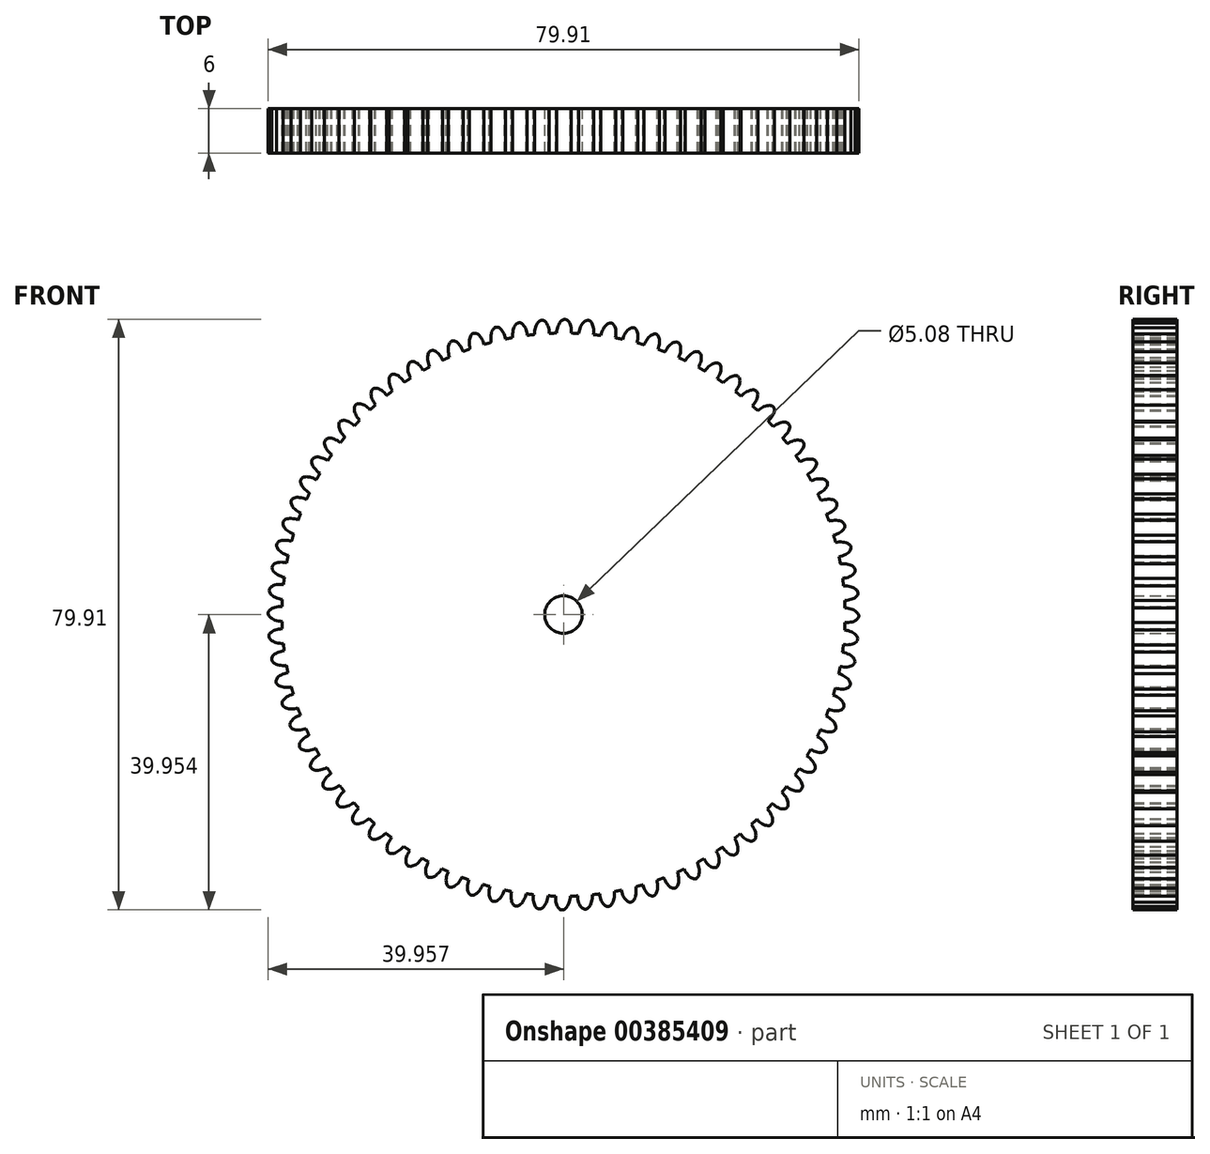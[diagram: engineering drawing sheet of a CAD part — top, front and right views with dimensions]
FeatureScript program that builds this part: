
annotation { "Feature Type Name" : "Feature", "Feature Type Description" : "" }
export const myFeature = defineFeature(function(context is Context, id is Id, definition is map)
    precondition{}
    {
        {
            var Q0;
            Q0=qCreatedBy(makeId("Front.planeOp"),FACE);
            var sketch = newSketch(context, id + "F0", { "sketchPlane" : qUnion([Q0])});
            skCircle(sketch, "E0", {"center": v(1.48, -19.42) * mm, "radius": 38.1 * mm});
            skCircle(sketch, "E1", {"center": v(1.48, -19.42) * mm, "radius": 2.54 * mm});
            skEllipticalArc(sketch, "E2", {});
            skEllipticalArc(sketch, "E3.1.0", {});
            skEllipticalArc(sketch, "E3.2.0", {});
            skEllipticalArc(sketch, "E3.3.0", {});
            skEllipticalArc(sketch, "E3.4.0", {});
            skEllipticalArc(sketch, "E3.5.0", {});
            skEllipticalArc(sketch, "E3.6.0", {});
            skEllipticalArc(sketch, "E3.7.0", {});
            skEllipticalArc(sketch, "E3.8.0", {});
            skEllipticalArc(sketch, "E3.9.0", {});
            skEllipticalArc(sketch, "E3.10.0", {});
            skEllipticalArc(sketch, "E3.11.0", {});
            skEllipticalArc(sketch, "E3.12.0", {});
            skEllipticalArc(sketch, "E3.13.0", {});
            skEllipticalArc(sketch, "E3.14.0", {});
            skEllipticalArc(sketch, "E3.15.0", {});
            skEllipticalArc(sketch, "E3.16.0", {});
            skEllipticalArc(sketch, "E3.17.0", {});
            skEllipticalArc(sketch, "E3.18.0", {});
            skEllipticalArc(sketch, "E3.19.0", {});
            skEllipticalArc(sketch, "E3.20.0", {});
            skEllipticalArc(sketch, "E3.21.0", {});
            skEllipticalArc(sketch, "E3.22.0", {});
            skEllipticalArc(sketch, "E3.23.0", {});
            skEllipticalArc(sketch, "E3.24.0", {});
            skEllipticalArc(sketch, "E3.25.0", {});
            skEllipticalArc(sketch, "E3.26.0", {});
            skEllipticalArc(sketch, "E3.27.0", {});
            skEllipticalArc(sketch, "E3.28.0", {});
            skEllipticalArc(sketch, "E3.29.0", {});
            skEllipticalArc(sketch, "E3.30.0", {});
            skEllipticalArc(sketch, "E3.31.0", {});
            skEllipticalArc(sketch, "E3.32.0", {});
            skEllipticalArc(sketch, "E3.33.0", {});
            skEllipticalArc(sketch, "E3.34.0", {});
            skEllipticalArc(sketch, "E3.35.0", {});
            skEllipticalArc(sketch, "E3.36.0", {});
            skEllipticalArc(sketch, "E3.37.0", {});
            skEllipticalArc(sketch, "E3.38.0", {});
            skEllipticalArc(sketch, "E3.39.0", {});
            skEllipticalArc(sketch, "E3.40.0", {});
            skEllipticalArc(sketch, "E3.41.0", {});
            skEllipticalArc(sketch, "E3.42.0", {});
            skEllipticalArc(sketch, "E3.43.0", {});
            skEllipticalArc(sketch, "E3.44.0", {});
            skEllipticalArc(sketch, "E3.45.0", {});
            skEllipticalArc(sketch, "E3.46.0", {});
            skEllipticalArc(sketch, "E3.47.0", {});
            skEllipticalArc(sketch, "E3.48.0", {});
            skEllipticalArc(sketch, "E3.49.0", {});
            skEllipticalArc(sketch, "E3.50.0", {});
            skEllipticalArc(sketch, "E3.51.0", {});
            skEllipticalArc(sketch, "E3.52.0", {});
            skEllipticalArc(sketch, "E3.53.0", {});
            skEllipticalArc(sketch, "E3.54.0", {});
            skEllipticalArc(sketch, "E3.55.0", {});
            skEllipticalArc(sketch, "E3.56.0", {});
            skEllipticalArc(sketch, "E3.57.0", {});
            skEllipticalArc(sketch, "E3.58.0", {});
            skEllipticalArc(sketch, "E3.59.0", {});
            skEllipticalArc(sketch, "E3.60.0", {});
            skEllipticalArc(sketch, "E3.61.0", {});
            skEllipticalArc(sketch, "E3.62.0", {});
            skEllipticalArc(sketch, "E3.63.0", {});
            skEllipticalArc(sketch, "E3.64.0", {});
            skEllipticalArc(sketch, "E3.65.0", {});
            skEllipticalArc(sketch, "E3.66.0", {});
            skEllipticalArc(sketch, "E3.67.0", {});
            skEllipticalArc(sketch, "E3.68.0", {});
            skEllipticalArc(sketch, "E3.69.0", {});
            skEllipticalArc(sketch, "E3.70.0", {});
            skEllipticalArc(sketch, "E3.71.0", {});
            skEllipticalArc(sketch, "E3.72.0", {});
            skEllipticalArc(sketch, "E3.73.0", {});
            skEllipticalArc(sketch, "E3.74.0", {});
            skEllipticalArc(sketch, "E3.75.0", {});
            skEllipticalArc(sketch, "E3.76.0", {});
            skEllipticalArc(sketch, "E3.77.0", {});
            skEllipticalArc(sketch, "E3.78.0", {});
            skEllipticalArc(sketch, "E3.79.0", {});
            const initialGuessF0  = {"E2": [-0.0014344001059815768, 0.018572813303266773, 0, -1, 0.0018570975044160444, 0.0009917459338206558, 1.604712424427073, 4.760295241054115], "E3.1.0": [-0.0044059786382855005, 0.018227300082595467, 0.07845909572784507, -0.996917333733128, 0.0018570975044160444, 0.0009917459338206558, 1.604712424427073, 4.760295241054115], "E3.2.0": [-0.007341288130832645, 0.017649704599345444, 0.15643446504023098, -0.9876883405951378, 0.0018570975044160444, 0.0009917459338206558, 1.604712424427073, 4.760295241054115], "E3.3.0": [-0.010222231424512, 0.016843587921740923, 0.2334453638559055, -0.9723699203976766, 0.0018570975044160444, 0.0009917459338206558, 1.604712424427073, 4.760295241054115], "E3.4.0": [-0.013031046545907171, 0.01581392002716034, 0.3090169943749475, -0.9510565162951535, 0.0018570975044160444, 0.0009917459338206558, 1.604712424427073, 4.760295241054115], "E3.5.0": [-0.015750416215768955, 0.014567049160573092, 0.3826834323650899, -0.9238795325112867, 0.0018570975044160444, 0.0009917459338206558, 1.604712424427073, 4.760295241054115], "E3.6.0": [-0.018363574615800467, 0.013110662695498342, 0.45399049973954686, -0.8910065241883678, 0.0018570975044160444, 0.0009917459338206558, 1.604712424427073, 4.760295241054115], "E3.7.0": [-0.020854410755502168, 0.011453739738790903, 0.522498564715949, -0.8526401643540923, 0.0018570975044160444, 0.0009917459338206558, 1.604712424427073, 4.760295241054115], "E3.8.0": [-0.02320756780178574, 0.009606495771461688, 0.5877852522924732, -0.8090169943749473, 0.0018570975044160444, 0.0009917459338206558, 1.604712424427073, 4.760295241054115], "E3.9.0": [-0.025408537758956712, 0.007580319666840222, 0.6494480483301838, -0.7604059656000308, 0.0018570975044160444, 0.0009917459338206558, 1.604712424427073, 4.760295241054115], "E3.10.0": [-0.027443750915332344, 0.005387703474383429, 0.7071067811865476, -0.7071067811865475, 0.0018570975044160444, 0.0009917459338206558, 1.604712424427073, 4.760295241054115], "E3.11.0": [-0.02930065950502653, 0.0030421654020366742, 0.7604059656000309, -0.6494480483301837, 0.0018570975044160444, 0.0009917459338206558, 1.604712424427073, 4.760295241054115], "E3.12.0": [-0.030967815069099056, 0.0005581664719865303, 0.8090169943749476, -0.587785252292473, 0.0018570975044160444, 0.0009917459338206558, 1.604712424427073, 4.760295241054115], "E3.13.0": [-0.032434939039111904, -0.002048978636349773, 0.8526401643540923, -0.5224985647159488, 0.0018570975044160444, 0.0009917459338206558, 1.604712424427073, 4.760295241054115], "E3.14.0": [-0.033692986107921735, -0.004763196006415627, 0.8910065241883679, -0.4539904997395467, 0.0018570975044160444, 0.0009917459338206558, 1.604712424427073, 4.760295241054115], "E3.15.0": [-0.03473419999700624, -0.0075677515855557004, 0.9238795325112867, -0.3826834323650897, 0.0018570975044160444, 0.0009917459338206558, 1.604712424427073, 4.760295241054115], "E3.16.0": [-0.035552161276500446, -0.010445354356015239, 0.9510565162951538, -0.3090169943749474, 0.0018570975044160444, 0.0009917459338206558, 1.604712424427073, 4.760295241054115], "E3.17.0": [-0.03614182694311655, -0.013378262939814329, 0.9723699203976768, -0.23344536385590542, 0.0018570975044160444, 0.0009917459338206558, 1.604712424427073, 4.760295241054115], "E3.18.0": [-0.036499561511936146, -0.016348394980242775, 0.9876883405951378, -0.1564344650402308, 0.0018570975044160444, 0.0009917459338206558, 1.604712424427073, 4.760295241054115], "E3.19.0": [-0.03662315943038362, -0.019337438625602218, 0.996917333733128, -0.07845909572784487, 0.0018570975044160444, 0.0009917459338206558, 1.604712424427073, 4.760295241054115], "E3.20.0": [-0.03651185867619128, -0.022326965427861133, 1, 0, 0.0018570975044160444, 0.0009917459338206558, 1.604712424427073, 4.760295241054115], "E3.21.0": [-0.03616634545551997, -0.025298543960165055, 0.996917333733128, 0.078459095727845, 0.0018570975044160444, 0.0009917459338206558, 1.604712424427073, 4.760295241054115], "E3.22.0": [-0.03558874997226995, -0.02823385345271219, 0.9876883405951378, 0.1564344650402307, 0.0018570975044160444, 0.0009917459338206558, 1.604712424427073, 4.760295241054115], "E3.23.0": [-0.03478263329466544, -0.031114796746391556, 0.9723699203976767, 0.23344536385590545, 0.0018570975044160444, 0.0009917459338206558, 1.604712424427073, 4.760295241054115], "E3.24.0": [-0.03375296540008485, -0.033923611867786724, 0.9510565162951536, 0.30901699437494745, 0.0018570975044160444, 0.0009917459338206558, 1.604712424427073, 4.760295241054115], "E3.25.0": [-0.0325060945334976, -0.03664298153764851, 0.9238795325112867, 0.38268343236508984, 0.0018570975044160444, 0.0009917459338206558, 1.604712424427073, 4.760295241054115], "E3.26.0": [-0.031049708068422846, -0.03925613993768002, 0.891006524188368, 0.4539904997395469, 0.0018570975044160444, 0.0009917459338206558, 1.604712424427073, 4.760295241054115], "E3.27.0": [-0.029392785111715412, -0.04174697607738173, 0.8526401643540922, 0.5224985647159489, 0.0018570975044160444, 0.0009917459338206558, 1.604712424427073, 4.760295241054115], "E3.28.0": [-0.027545541144386194, -0.04410013312366529, 0.8090169943749476, 0.5877852522924732, 0.0018570975044160441, 0.0009917459338206556, 1.604712424427073, 4.760295241054115], "E3.29.0": [-0.025519365039764735, -0.046301103080836264, 0.7604059656000309, 0.6494480483301837, 0.0018570975044160444, 0.0009917459338206558, 1.604712424427073, 4.760295241054115], "E3.30.0": [-0.023326748847307933, -0.0483363162372119, 0.7071067811865475, 0.7071067811865476, 0.0018570975044160444, 0.0009917459338206558, 1.604712424427073, 4.760295241054115], "E3.31.0": [-0.02098121077496118, -0.050193224826906094, 0.6494480483301837, 0.760405965600031, 0.0018570975044160444, 0.0009917459338206558, 1.604712424427073, 4.760295241054115], "E3.32.0": [-0.01849721184491104, -0.05186038039097861, 0.5877852522924731, 0.8090169943749475, 0.0018570975044160444, 0.0009917459338206558, 1.604712424427073, 4.760295241054115], "E3.33.0": [-0.015890066736574733, -0.05332750436099146, 0.5224985647159488, 0.8526401643540923, 0.0018570975044160444, 0.0009917459338206558, 1.604712424427073, 4.760295241054115], "E3.34.0": [-0.013175849366508884, -0.054585551429801295, 0.45399049973954675, 0.8910065241883679, 0.0018570975044160444, 0.0009917459338206558, 1.604712424427073, 4.760295241054115], "E3.35.0": [-0.010371293787368807, -0.0556267653188858, 0.3826834323650898, 0.9238795325112867, 0.0018570975044160444, 0.0009917459338206558, 1.604712424427073, 4.760295241054115], "E3.36.0": [-0.00749369101690927, -0.056444726598380006, 0.30901699437494745, 0.9510565162951538, 0.0018570975044160444, 0.0009917459338206558, 1.604712424427073, 4.760295241054115], "E3.37.0": [-0.004560782433110183, -0.05703439226499611, 0.23344536385590542, 0.9723699203976766, 0.0018570975044160444, 0.0009917459338206558, 1.604712424427073, 4.760295241054115], "E3.38.0": [-0.0015906503926817327, -0.0573921268338157, 0.1564344650402309, 0.9876883405951379, 0.0018570975044160444, 0.0009917459338206558, 1.604712424427073, 4.760295241054115], "E3.39.0": [0.0013983932526777068, -0.05751572475226318, 0.07845909572784494, 0.996917333733128, 0.0018570975044160444, 0.0009917459338206558, 1.604712424427073, 4.760295241054115], "E3.40.0": [0.004387920054936623, -0.05740442399807084, 0, 1, 0.0018570975044160444, 0.0009917459338206558, 1.604712424427073, 4.760295241054115], "E3.41.0": [0.0073594985872405295, -0.057058910777399545, -0.0784590957278445, 0.9969173337331281, 0.0018570975044160444, 0.0009917459338206558, 1.604712424427073, 4.760295241054115], "E3.42.0": [0.01029480807978769, -0.0564813152941495, -0.15643446504023084, 0.9876883405951378, 0.0018570975044160444, 0.0009917459338206558, 1.604712424427073, 4.760295241054115], "E3.43.0": [0.013175751373467045, -0.05567519861654499, -0.2334453638559054, 0.9723699203976767, 0.0018570975044160444, 0.0009917459338206558, 1.604712424427073, 4.760295241054115], "E3.44.0": [0.015984566494862205, -0.054645530721964417, -0.309016994374947, 0.9510565162951538, 0.0018570975044160444, 0.0009917459338206558, 1.604712424427073, 4.760295241054115], "E3.45.0": [0.018703936164724003, -0.05339865985537716, -0.3826834323650898, 0.9238795325112868, 0.0018570975044160444, 0.0009917459338206558, 1.604712424427073, 4.760295241054115], "E3.46.0": [0.021317094564755515, -0.05194227339030241, -0.4539904997395469, 0.891006524188368, 0.0018570975044160444, 0.0009917459338206558, 1.604712424427073, 4.760295241054115], "E3.47.0": [0.023807930704457234, -0.05028535043359496, -0.5224985647159492, 0.852640164354092, 0.0018570975044160444, 0.0009917459338206558, 1.604712424427073, 4.760295241054115], "E3.48.0": [0.02616108775074079, -0.04843810646626576, -0.5877852522924731, 0.8090169943749475, 0.0018570975044160444, 0.0009917459338206558, 1.604712424427073, 4.760295241054115], "E3.49.0": [0.028362057707911746, -0.0464119303616443, -0.6494480483301833, 0.7604059656000313, 0.0018570975044160444, 0.0009917459338206558, 1.604712424427073, 4.760295241054115], "E3.50.0": [0.030397270864287396, -0.04421931416918749, -0.7071067811865476, 0.7071067811865476, 0.0018570975044160444, 0.0009917459338206558, 1.604712424427073, 4.760295241054115], "E3.51.0": [0.032254179453981575, -0.04187377609684076, -0.7604059656000307, 0.649448048330184, 0.0018570975044160444, 0.0009917459338206558, 1.604712424427073, 4.760295241054115], "E3.52.0": [0.0339213350180541, -0.039389777166790596, -0.8090169943749475, 0.5877852522924731, 0.0018570975044160444, 0.0009917459338206558, 1.604712424427073, 4.760295241054115], "E3.53.0": [0.03538845898806696, -0.03678263205845428, -0.8526401643540925, 0.5224985647159485, 0.0018570975044160444, 0.0009917459338206558, 1.604712424427073, 4.760295241054115], "E3.54.0": [0.03664650605687679, -0.03406841468838844, -0.8910065241883679, 0.4539904997395468, 0.0018570975044160444, 0.0009917459338206558, 1.604712424427073, 4.760295241054115], "E3.55.0": [0.03768771994596129, -0.03126385910924835, -0.9238795325112871, 0.3826834323650895, 0.0018570975044160444, 0.0009917459338206558, 1.604712424427073, 4.760295241054115], "E3.56.0": [0.0385056812254555, -0.02838625633878883, -0.9510565162951538, 0.3090169943749475, 0.0018570975044160444, 0.0009917459338206558, 1.604712424427073, 4.760295241054115], "E3.57.0": [0.0390953468920716, -0.02545334775498976, -0.9723699203976764, 0.2334453638559059, 0.0018570975044160444, 0.0009917459338206558, 1.604712424427073, 4.760295241054115], "E3.58.0": [0.03945308146089119, -0.02248321571456129, -0.9876883405951379, 0.15643446504023095, 0.0018570975044160441, 0.0009917459338206556, 1.604712424427073, 4.760295241054115], "E3.59.0": [0.039576679379338675, -0.01949417206920187, -0.996917333733128, 0.07845909572784544, 0.0018570975044160444, 0.0009917459338206558, 1.604712424427073, 4.760295241054115], "E3.60.0": [0.03946537862514633, -0.01650464526694294, -1, 0, 0.0018570975044160444, 0.0009917459338206558, 1.604712424427073, 4.760295241054115], "E3.61.0": [0.03911986540447503, -0.013533066734638995, -0.996917333733128, -0.07845909572784533, 0.0018570975044160444, 0.0009917459338206558, 1.604712424427073, 4.760295241054115], "E3.62.0": [0.038542269921225, -0.01059775724209187, -0.9876883405951378, -0.15643446504023079, 0.0018570975044160444, 0.0009917459338206558, 1.604712424427073, 4.760295241054115], "E3.63.0": [0.03773615324362048, -0.007716813948412497, -0.9723699203976766, -0.23344536385590578, 0.0018570975044160444, 0.0009917459338206558, 1.604712424427073, 4.760295241054115], "E3.64.0": [0.03670648534903989, -0.004907998827017342, -0.9510565162951536, -0.30901699437494734, 0.0018570975044160444, 0.0009917459338206558, 1.604712424427073, 4.760295241054115], "E3.65.0": [0.03545961448245266, -0.002188629157155576, -0.923879532511287, -0.3826834323650893, 0.0018570975044160444, 0.0009917459338206558, 1.604712424427073, 4.760295241054115], "E3.66.0": [0.0340032280173779, 0.0004245292428759536, -0.891006524188368, -0.45399049973954686, 0.0018570975044160444, 0.0009917459338206558, 1.604712424427073, 4.760295241054115], "E3.67.0": [0.032346305060670474, 0.0029153653825776463, -0.8526401643540926, -0.5224985647159486, 0.0018570975044160444, 0.0009917459338206558, 1.604712424427073, 4.760295241054115], "E3.68.0": [0.03049906109334125, 0.0052685224288612255, -0.8090169943749477, -0.5877852522924731, 0.0018570975044160444, 0.0009917459338206558, 1.604712424427073, 4.760295241054115], "E3.69.0": [0.02847288498871977, 0.007469492386032214, -0.7604059656000307, -0.649448048330184, 0.0018570975044160444, 0.0009917459338206558, 1.604712424427073, 4.760295241054115], "E3.70.0": [0.02628026879626299, 0.009504705542407833, -0.7071067811865476, -0.7071067811865475, 0.0018570975044160444, 0.0009917459338206558, 1.604712424427073, 4.760295241054115], "E3.71.0": [0.02393473072391622, 0.011361614132102033, -0.6494480483301833, -0.7604059656000312, 0.0018570975044160444, 0.0009917459338206558, 1.604712424427073, 4.760295241054115], "E3.72.0": [0.021450731793866095, 0.013028769696174544, -0.5877852522924732, -0.8090169943749475, 0.0018570975044160444, 0.0009917459338206558, 1.604712424427073, 4.760295241054115], "E3.73.0": [0.018843586685529806, 0.014495893666187386, -0.5224985647159494, -0.852640164354092, 0.0018570975044160444, 0.0009917459338206558, 1.604712424427073, 4.760295241054115], "E3.74.0": [0.016129369315463937, 0.01575394073499723, -0.45399049973954686, -0.8910065241883679, 0.0018570975044160444, 0.0009917459338206558, 1.604712424427073, 4.760295241054115], "E3.75.0": [0.013324813736323878, 0.016795154624081727, -0.3826834323650904, -0.9238795325112867, 0.0018570975044160444, 0.0009917459338206558, 1.604712424427073, 4.760295241054115], "E3.76.0": [0.010447210965864324, 0.017613115903575942, -0.3090169943749475, -0.9510565162951535, 0.0018570975044160444, 0.0009917459338206558, 1.604712424427073, 4.760295241054115], "E3.77.0": [0.0075143023820652185, 0.01820278157019205, -0.23344536385590514, -0.9723699203976769, 0.0018570975044160444, 0.0009917459338206558, 1.604712424427073, 4.760295241054115], "E3.78.0": [0.004544170341636788, 0.018560516139011635, -0.156434465040231, -0.9876883405951379, 0.0018570975044160444, 0.0009917459338206558, 1.604712424427073, 4.760295241054115], "E3.79.0": [0.0015551266962773314, 0.018684114057459116, -0.07845909572784462, -0.996917333733128, 0.0018570975044160444, 0.0009917459338206558, 1.604712424427073, 4.760295241054115]};
            skSetInitialGuess(sketch, initialGuessF0);
            skSolve(sketch);
        }
        {
            var Q0;
            Q0=qSketchRegion(id+"F0",true);
            extrude(context, id + "F1", {"entities" : qUnion([Q0]), "depth" : 6 * mm});
        }
    });
